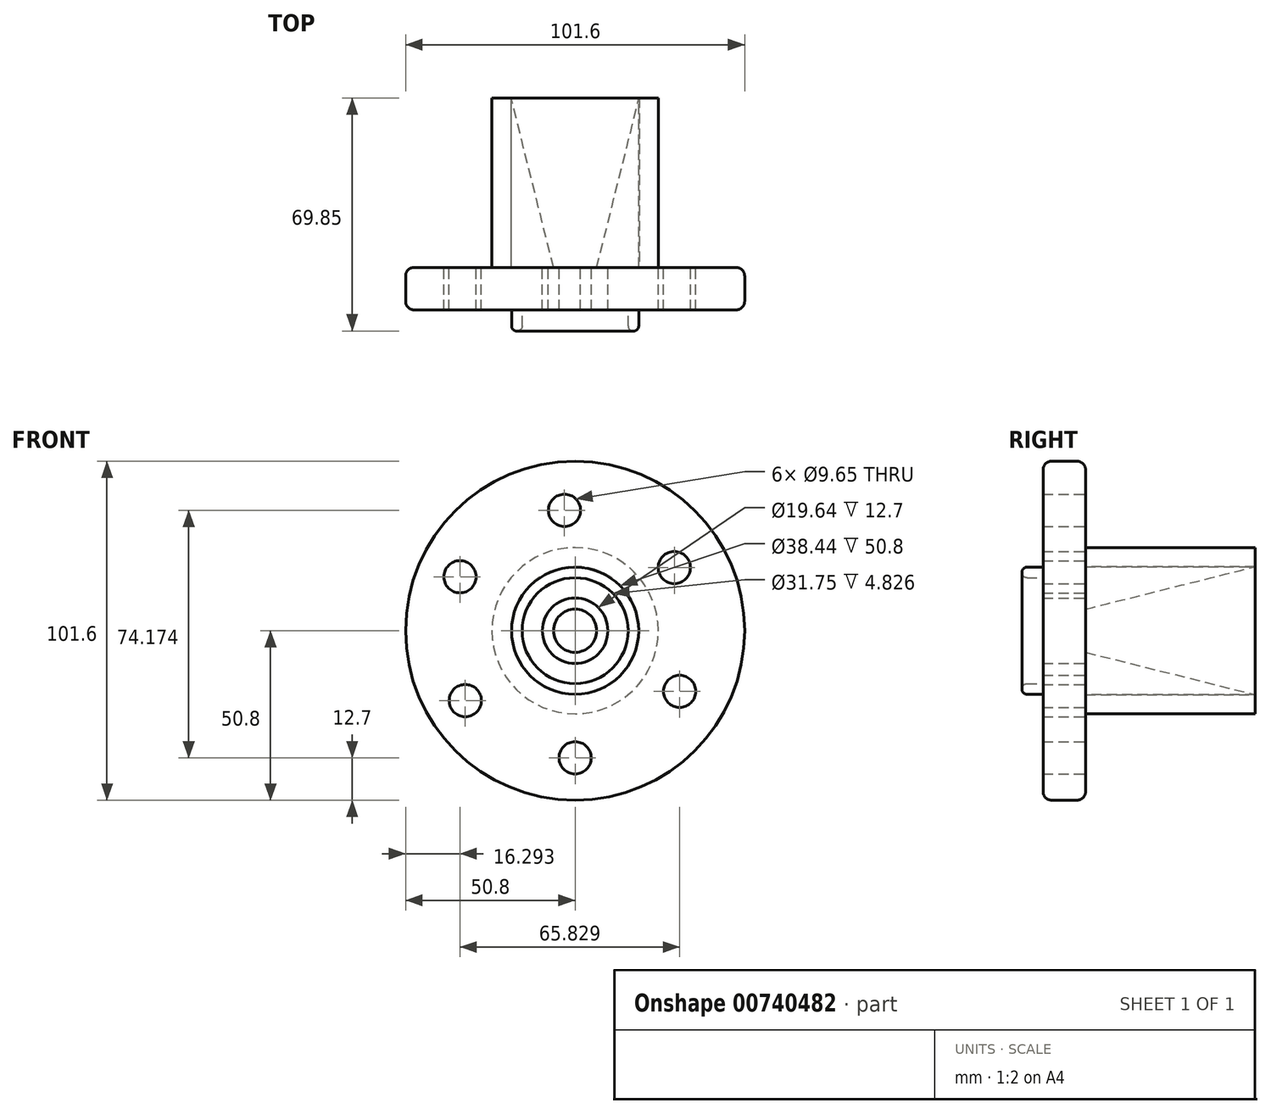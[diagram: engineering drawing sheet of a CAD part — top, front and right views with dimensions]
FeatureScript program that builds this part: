
annotation { "Feature Type Name" : "Feature", "Feature Type Description" : "" }
export const myFeature = defineFeature(function(context is Context, id is Id, definition is map)
    precondition{}
    {
        {
            var Q0;
            Q0=qCreatedBy(makeId("Front.planeOp"),FACE);
            var sketch = newSketch(context, id + "F0", { "sketchPlane" : qUnion([Q0])});
            skCircle(sketch, "E0", {"center": v(0, 0) * mm, "radius": 50.8 * mm});
            skCircle(sketch, "E1", {"center": v(0, 0) * mm, "radius": 24.42 * mm});
            skCircle(sketch, "E2", {"center": v(0, 0) * mm, "radius": 14.7 * mm});
            skCircle(sketch, "E3", {"center": v(0, 0) * mm, "radius": 9.82 * mm});
            skLineSegment(sketch, "E4.0", {"start": v(0, -38.1) * mm, "end": v(-32.91, -20.94) * mm});
            skLineSegment(sketch, "E4.1", {"start": v(-32.91, -20.94) * mm, "end": v(-34.5, 16.15) * mm});
            skLineSegment(sketch, "E4.2", {"start": v(-34.5, 16.15) * mm, "end": v(-3.18, 36.07) * mm});
            skLineSegment(sketch, "E4.3", {"start": v(-3.18, 36.07) * mm, "end": v(29.73, 18.9) * mm});
            skLineSegment(sketch, "E4.4", {"start": v(29.73, 18.9) * mm, "end": v(31.32, -18.18) * mm});
            skLineSegment(sketch, "E4.5", {"start": v(31.32, -18.18) * mm, "end": v(0, -38.1) * mm});
            skCircle(sketch, "E5", {"center": v(-3.18, 36.07) * mm, "radius": 4.82 * mm});
            skCircle(sketch, "E6", {"center": v(-34.5, 16.15) * mm, "radius": 4.82 * mm});
            skCircle(sketch, "E7", {"center": v(29.73, 18.9) * mm, "radius": 4.82 * mm});
            skCircle(sketch, "E8", {"center": v(0, -38.1) * mm, "radius": 4.82 * mm});
            skCircle(sketch, "E9", {"center": v(31.32, -18.18) * mm, "radius": 4.82 * mm});
            skCircle(sketch, "E10", {"center": v(-32.91, -20.94) * mm, "radius": 4.82 * mm});
            skCircle(sketch, "E11", {"center": v(0, 0) * mm, "radius": 38.1 * mm});
            skSolve(sketch);
        }
        {
            var Q0;
            Q0=makeQuery(id+"F0.imprint","IMPRINT",FACE,{"disambiguationData":[TD([[makeQuery(id+"F0.imprint","IMPRINT",EDGE,{"derivedFrom":sQuery(id+"F0.wireOp",EDGE,"E0")}),1.0]])]});
            var Q1;
            Q1=makeQuery(id+"F0.imprint","IMPRINT",FACE,{"disambiguationData":[TD([[makeQuery(id+"F0.imprint","IMPRINT",EDGE,{"derivedFrom":sQuery(id+"F0.wireOp",EDGE,"E1")}),-1.0]])]});
            var Q2;
            Q2=makeQuery(id+"F0.imprint","IMPRINT",FACE,{"disambiguationData":[TD([[makeQuery(id+"F0.imprint","IMPRINT",EDGE,{"derivedFrom":sQuery(id+"F0.wireOp",EDGE,"E1")}),1.0]])]});
            var Q3;
            Q3=makeQuery(id+"F0.imprint","IMPRINT",FACE,{"disambiguationData":[TD([[makeQuery(id+"F0.imprint","IMPRINT",EDGE,{"derivedFrom":sQuery(id+"F0.wireOp",EDGE,"E2")}),1.0]])]});
            var Q4;
            {var subQ0=sQuery(id+"F0.wireOp",EDGE,"E7");var subQ1=sQuery(id+"F0.wireOp",EDGE,"E4.4");var subQ2=makeQuery(id+"F0.imprint","INTERSECT",VERTEX,{"derivedFrom":[subQ1,subQ0]});Q4=makeQuery(id+"F0.imprint","IMPRINT",FACE,{"disambiguationData":[TD([[makeQuery(id+"F0.imprint","IMPRINT",EDGE,{"disambiguationData":[TD([[subQ2,-1.0]])],"derivedFrom":subQ1}),1.0]])]});}
            var Q5;
            {var subQ0=sQuery(id+"F0.wireOp",EDGE,"E9");var subQ1=sQuery(id+"F0.wireOp",EDGE,"E4.5");var subQ2=makeQuery(id+"F0.imprint","INTERSECT",VERTEX,{"derivedFrom":[subQ1,subQ0]});Q5=makeQuery(id+"F0.imprint","IMPRINT",FACE,{"disambiguationData":[TD([[makeQuery(id+"F0.imprint","IMPRINT",EDGE,{"disambiguationData":[TD([[subQ2,-1.0]])],"derivedFrom":subQ1}),1.0]])]});}
            var Q6;
            {var subQ0=sQuery(id+"F0.wireOp",EDGE,"E8");var subQ1=sQuery(id+"F0.wireOp",EDGE,"E4.0");var subQ2=makeQuery(id+"F0.imprint","INTERSECT",VERTEX,{"derivedFrom":[subQ1,subQ0]});Q6=makeQuery(id+"F0.imprint","IMPRINT",FACE,{"disambiguationData":[TD([[makeQuery(id+"F0.imprint","IMPRINT",EDGE,{"disambiguationData":[TD([[subQ2,-1.0]])],"derivedFrom":subQ1}),1.0]])]});}
            var Q7;
            {var subQ0=sQuery(id+"F0.wireOp",EDGE,"E10");var subQ1=sQuery(id+"F0.wireOp",EDGE,"E4.1");var subQ2=makeQuery(id+"F0.imprint","INTERSECT",VERTEX,{"derivedFrom":[subQ1,subQ0]});Q7=makeQuery(id+"F0.imprint","IMPRINT",FACE,{"disambiguationData":[TD([[makeQuery(id+"F0.imprint","IMPRINT",EDGE,{"disambiguationData":[TD([[subQ2,-1.0]])],"derivedFrom":subQ1}),1.0]])]});}
            var Q8;
            {var subQ0=sQuery(id+"F0.wireOp",EDGE,"E6");var subQ1=sQuery(id+"F0.wireOp",EDGE,"E4.2");var subQ2=makeQuery(id+"F0.imprint","INTERSECT",VERTEX,{"derivedFrom":[subQ1,subQ0]});Q8=makeQuery(id+"F0.imprint","IMPRINT",FACE,{"disambiguationData":[TD([[makeQuery(id+"F0.imprint","IMPRINT",EDGE,{"disambiguationData":[TD([[subQ2,-1.0]])],"derivedFrom":subQ1}),1.0]])]});}
            var Q9;
            {var subQ0=sQuery(id+"F0.wireOp",EDGE,"E5");var subQ1=sQuery(id+"F0.wireOp",EDGE,"E4.3");var subQ2=makeQuery(id+"F0.imprint","INTERSECT",VERTEX,{"derivedFrom":[subQ1,subQ0]});Q9=makeQuery(id+"F0.imprint","IMPRINT",FACE,{"disambiguationData":[TD([[makeQuery(id+"F0.imprint","IMPRINT",EDGE,{"disambiguationData":[TD([[subQ2,-1.0]])],"derivedFrom":subQ1}),1.0]])]});}
            var Q10;
            Q10=sQuery(id+"F0.wireOp",EDGE,"E0");
            extrude(context, id + "F1", {"entities" : qUnion([Q0, Q1, Q2, Q3, Q4, Q5, Q6, Q7, Q8, Q9]), "surfaceEntities" : qUnion([Q10]), "depth" : 12.7 * mm, "offsetDistance" : 25.4 * mm});
        }
        {
            var Q0;
            Q0=qCreatedBy(makeId("Front.planeOp"),FACE);
            var sketch = newSketch(context, id + "F2", { "sketchPlane" : qUnion([Q0])});
            skCircle(sketch, "E12", {"center": v(0, 0) * mm, "radius": 24.92 * mm});
            skCircle(sketch, "E13", {"center": v(0, 0) * mm, "radius": 19.22 * mm});
            skCircle(sketch, "E14", {"center": v(0, 0) * mm, "radius": 5.54 * mm});
            skSolve(sketch);
        }
        {
            var Q0;
            Q0=makeQuery(id+"F2.imprint","IMPRINT",FACE,{"disambiguationData":[TD([[makeQuery(id+"F2.imprint","IMPRINT",EDGE,{"derivedFrom":sQuery(id+"F2.wireOp",EDGE,"E12")}),1.0]])]});
            extrude(context, id + "F3", {"entities" : qUnion([Q0]), "operationType" : NewBodyOperationType.ADD, "oppositeDirection" : true, "depth" : 50.8 * mm, "offsetDistance" : 25.4 * mm});
        }
        {
            var Q0;
            Q0=makeQuery(id+"F3.opExtrude","CAP_FACE",FACE,{"disambiguationData":[OSD([sQuery(id+"F2.wireOp",EDGE,"E12"),sQuery(id+"F2.wireOp",EDGE,"E13")])],"isStart":false});
            var sketch = newSketch(context, id + "F4", { "sketchPlane" : qUnion([Q0])});
            skCircle(sketch, "E15", {"center": v(0, 0) * mm, "radius": 19.22 * mm});
            skCircle(sketch, "E16", {"center": v(0, 0) * mm, "radius": 6.85 * mm});
            skSolve(sketch);
        }
        {
            var Q0;
            Q0=qCreatedBy(makeId("Right.planeOp"),FACE);
            var sketch = newSketch(context, id + "F5", { "sketchPlane" : qUnion([Q0])});
            skLineSegment(sketch, "E17", {"start": v(0, -6.47) * mm, "end": v(50.8, -19.17) * mm});
            skLineSegment(sketch, "E18", {"start": v(50.8, -19.17) * mm, "end": v(0, -19.17) * mm});
            skLineSegment(sketch, "E19", {"start": v(0, -19.17) * mm, "end": v(0, -6.47) * mm});
            skLineSegment(sketch, "E20", {"start": v(51.45, 0) * mm, "end": v(0, 0) * mm});
            skSolve(sketch);
        }
        {
            var Q0;
            Q0 = qSketchRegion(id + "F5", true);
            var Q1;
            Q1=sQuery(id+"F5.wireOp",EDGE,"E20");
            revolve(context, id + "F6", {"operationType" : NewBodyOperationType.ADD, "surfaceOperationType" : NewSurfaceOperationType.NEW, "entities" : qUnion([Q0]), "axis" : qUnion([Q1]), "revolveType" : RevolveType.FULL});
        }
        {
            var Q0;
            Q0=makeQuery(id+"F1.opExtrude","CAP_FACE",FACE,{"disambiguationData":[OSD([sQuery(id+"F0.wireOp",EDGE,"E0"),sQuery(id+"F0.wireOp",EDGE,"E3"),sQuery(id+"F0.wireOp",EDGE,"E5"),sQuery(id+"F0.wireOp",EDGE,"E6"),sQuery(id+"F0.wireOp",EDGE,"E7"),sQuery(id+"F0.wireOp",EDGE,"E8"),sQuery(id+"F0.wireOp",EDGE,"E9"),sQuery(id+"F0.wireOp",EDGE,"E10")])],"isStart":false});
            var sketch = newSketch(context, id + "F7", { "sketchPlane" : qUnion([Q0])});
            skCircle(sketch, "E21", {"center": v(0, 0) * mm, "radius": 19.05 * mm});
            skCircle(sketch, "E22", {"center": v(0, 0) * mm, "radius": 15.88 * mm});
            skSolve(sketch);
        }
        {
            var Q0;
            Q0 = qSketchRegion(id + "F7", true);
            extrude(context, id + "F8", {"entities" : qUnion([Q0]), "operationType" : NewBodyOperationType.ADD, "depth" : 6.35 * mm, "offsetDistance" : 25.4 * mm});
        }
        {
            var Q0;
            Q0=makeQuery(id+"F8.opExtrude","CAP_EDGE",EDGE,{"disambiguationData":[OSD([sQuery(id+"F7.wireOp",EDGE,"E21")])],"isStart":false});
            var Q1;
            Q1=makeQuery(id+"F8.opExtrude","CAP_EDGE",EDGE,{"disambiguationData":[OSD([sQuery(id+"F7.wireOp",EDGE,"E22")])],"isStart":false});
            fillet(context, id + "F9", {"entities" : qUnion([Q0, Q1]), "radius" : 1.52 * mm, "tangentPropagation" : true, "allowEdgeOverflow" : false});
        }
        {
            var Q0;
            Q0=makeQuery(id+"F1.opExtrude","CAP_EDGE",EDGE,{"disambiguationData":[OSD([sQuery(id+"F0.wireOp",EDGE,"E0")])],"isStart":false});
            var Q1;
            Q1=makeQuery(id+"F1.opExtrude","CAP_EDGE",EDGE,{"disambiguationData":[OSD([sQuery(id+"F0.wireOp",EDGE,"E0")])],"isStart":true});
            fillet(context, id + "F10", {"entities" : qUnion([Q0, Q1]), "radius" : 2.54 * mm, "tangentPropagation" : true, "allowEdgeOverflow" : false});
        }
    });
